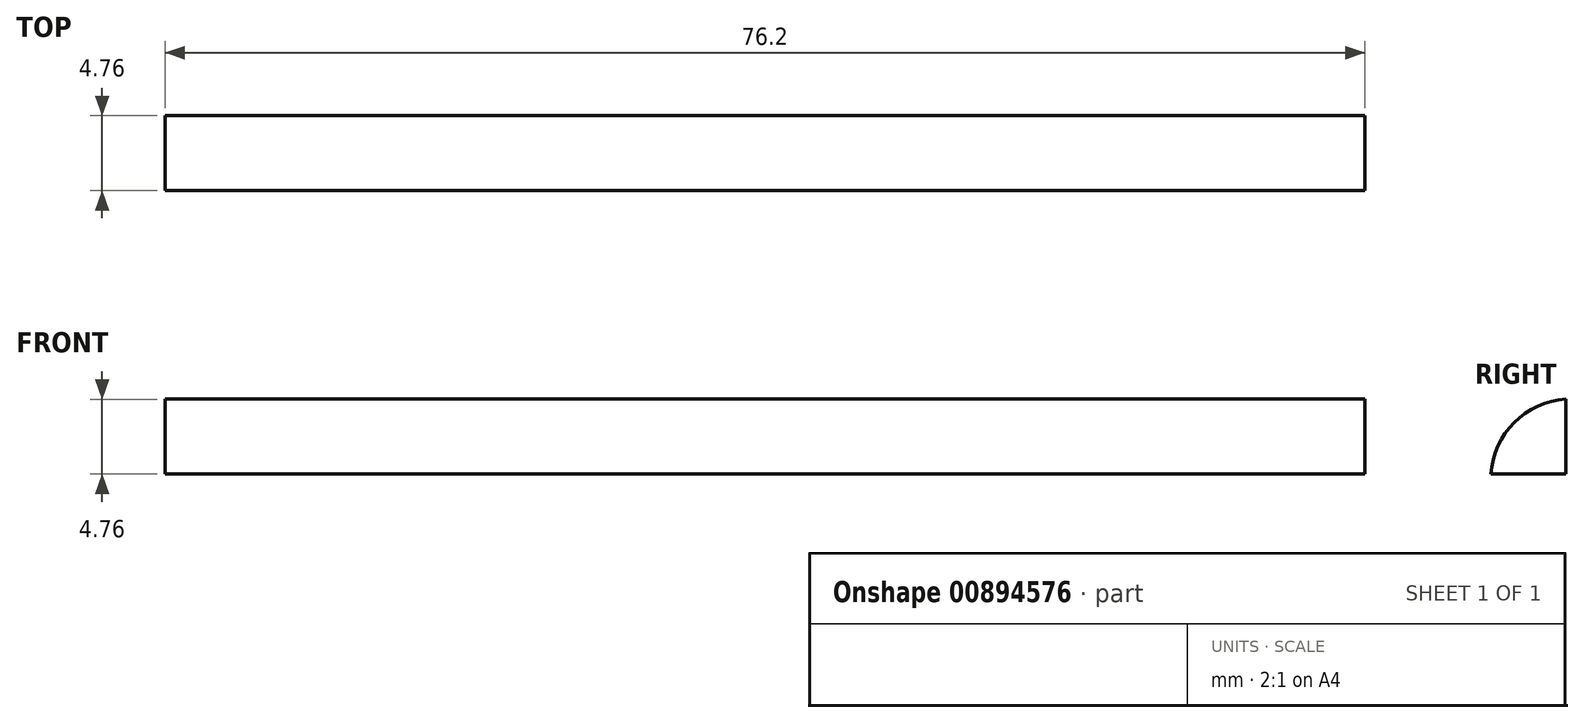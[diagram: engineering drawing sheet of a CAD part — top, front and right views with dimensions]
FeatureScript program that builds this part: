
annotation { "Feature Type Name" : "Feature", "Feature Type Description" : "" }
export const myFeature = defineFeature(function(context is Context, id is Id, definition is map)
    precondition{}
    {
        {
            var Q0;
            Q0=qCreatedBy(makeId("Right.planeOp"),FACE);
            var sketch = newSketch(context, id + "F0", { "sketchPlane" : qUnion([Q0])});
            skLineSegment(sketch, "E0", {"start": v(0, 0) * mm, "end": v(-4.76, 0) * mm});
            skLineSegment(sketch, "E1", {"start": v(0, 0) * mm, "end": v(0, 4.76) * mm});
            skArc(sketch, "E2", {"start": v(0, 4.76) * mm, "mid": v(-3.28, 3.28) * mm, "end": v(-4.76, 0) * mm});
            skSolve(sketch);
        }
        {
            var Q0;
            Q0 = qSketchRegion(id + "F0", true);
            extrude(context, id + "F1", {"entities" : qUnion([Q0]), "depth" : 76.2 * mm, "offsetDistance" : 25.4 * mm});
        }
    });
